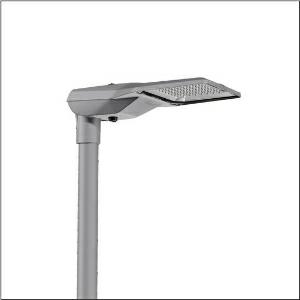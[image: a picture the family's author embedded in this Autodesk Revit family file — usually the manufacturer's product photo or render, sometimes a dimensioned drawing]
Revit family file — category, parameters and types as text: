
# Revit family: streetlight_sl_21_midi___st0_8a_5xe3c43t08nb_aee1
name_source: partatom
category: Lighting Fixtures
units: mm (PartAtom-declared; Revit-internal decimal feet)

## family parameters
Cut with Voids When Loaded = No
Host = Face
Light Source = No
Part Type = Normal
Room Calculation Point = No
Round Connector Dimension = Use Diameter
Shared = No

## types (1)
- --- (1 x LED, 23710 lm, 151.2 W, 4000K)
    Apparent Load = 151 VA
    CIE Flux Codes = 41 75 97 100 100
    Color Rendering = 70
    Color Temperature = 4000K
    Default Elevation = 1800 mm
    Description = Streetlight SL 21 midi, mast luminaire, primary light control with lens, of PMMA, primary optical cover: cover, of toughened safety glass, transparent, light distribution: ST0.8a, light emission: direct distribution, primary light characteristic: asymmetric, installation type: side-entry, post-top, LED, High Power LED, rated luminous flux: 23.710lm, luminous efficacy: 157lm/W, light colour: 740, colour temperature: 4000K, control gear: D4i, control: overheat protection, constant luminous flux control, time-dependent luminous flux control, flexible luminous flux parameterisation, pre-setting: logarithmic dimming characteristic, mains connection: 230..240V, AC, 50/60Hz, start of lifetime: 151W, end of service life: 157W, reduction: 70W, luminaire housing, of diecast aluminium, powder-coated, SITECO metallic grey (DB 702S), corrosivity category C5 high according to DIN EN ISO 12944, please order mast flange separately, inclination adjustable: 0°, 5°, 10°, 15°, sealing non-destructively replaceable, multi-level sealing system, length: 644mm, width: 335mm, height: 110mm, mast flange for spigot size: 42mm (side-entry): 5XC10008XM4, 60/48mm (side-entry/post-top): 5XC10108XM2, 76/60mm (side-entry/post-top): 5XC10108XM1, mounting height: 4..8m, Smart Interface below and above, protection rating (complete): IP66, insulation class (complete): insulation class II (safety insulation), certification: CE, ENEC, ENEC+, VDE, impact resistance: IK10, permissible operating ambient temperature for outdoor applications: -40..+50°C, standard-compliant lighting for roads and squares, packaging unit: 1 piece

Light Distribution: ST0.8a
    Height = 111 mm
    Lamp = 1 x LED
    Lamp Light Flux = 23710 lm
    Lamp Power = 151.2 W
    Lamp count = 1
    Length = 644 mm
    Luminous efficacy = 157 lm/W
    Manufacturer = Siteco
    ModVariant = No
    Model = 5XE3C43T08NB
    Number of Poles = 1
    OnlyDefault = Yes
    Power Factor = 1
    Product Name = Streetlight SL 21 midi | ST0.8a
    Product group = mast luminaire | pylon top
    ProductGroupID = 6100
    Protection Class = Protection class II
    Protection Degree = IP 66
    RLX_Detail_Level = 1
    RLX_Emergency_Light_Flux = 0 lm
    RLX_Emergency_Type = 0
    RLX_Emergency_Type_DB = No
    RlxData = <blob elided: 26997 chars, md5=c4113e73>
    Socket = socket
    Standby Power = 0 W
    System Light Flux = 23710 lm
    System Power = 151 W
    Type Comments = factory setting: luminous flux: 100 % | dim-lin: 254 | 802 mA
    Type Image = l_1004304.jpg
    URL = http://relux.com
    VarID = @adj_168083
    Voltage = 0 V
    Weight = 0.00 kg
    Width = 336 mm

## geometry (parser evidence)
native form markers: Blend x4, Sweep x9
no freeform markers — native parametric forms only
